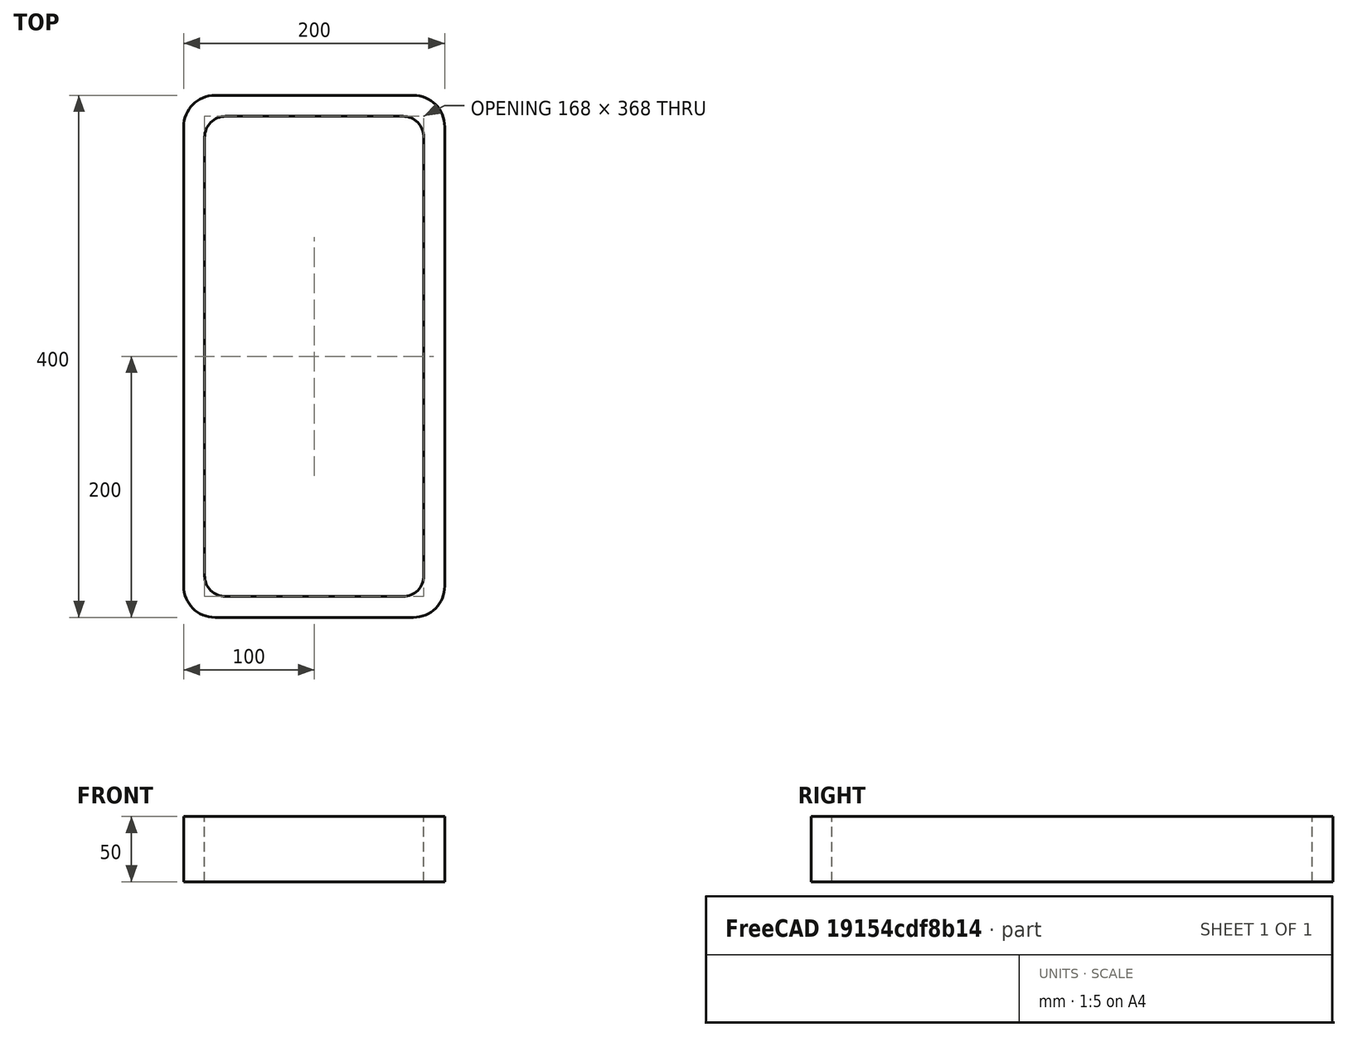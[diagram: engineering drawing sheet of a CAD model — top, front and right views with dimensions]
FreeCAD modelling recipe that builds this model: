
FCSTD DOCUMENT  (FreeCAD 0.15R4671 (Git))
Label: Rectangular hollow section 400x200x16 EN10219 S235JRH
License: All rights reserved
LicenseURL: http://en.wikipedia.org/wiki/All_rights_reserved
objects: Sketcher::SketchObject×1, Part::Extrusion×1
note: 2 computed .brp shape members not serialized (recipe doc carries the construction recipe); baked Part::Feature solids carry a one-line shape summary decoded from their .brp

FEATURE [Sketcher::SketchObject] Sketch
  sketch-geometry (16):
    g0: LineSegment StartX=-68 StartY=184 StartZ=0 EndX=68 EndY=184 EndZ=0
    g1: LineSegment StartX=84 StartY=168 StartZ=0 EndX=84 EndY=-168 EndZ=0
    g2: LineSegment StartX=68 StartY=-184 StartZ=0 EndX=-68 EndY=-184 EndZ=0
    g3: LineSegment StartX=-84 StartY=-168 StartZ=0 EndX=-84 EndY=168 EndZ=0
    g4: LineSegment StartX=-76 StartY=200 StartZ=0 EndX=76 EndY=200 EndZ=0
    g5: LineSegment StartX=100 StartY=176 StartZ=0 EndX=100 EndY=-176 EndZ=0
    g6: LineSegment StartX=76 StartY=-200 StartZ=0 EndX=-76 EndY=-200 EndZ=0
    g7: LineSegment StartX=-100 StartY=-176 StartZ=0 EndX=-100 EndY=176 EndZ=0
    g8: ArcOfCircle CenterX=-68 CenterY=168 CenterZ=0 NormalX=0 NormalY=0 NormalZ=1 Radius=16 StartAngle=1.5708 EndAngle=3.14159
    g9: ArcOfCircle CenterX=68 CenterY=168 CenterZ=0 NormalX=0 NormalY=0 NormalZ=1 Radius=16 StartAngle=0 EndAngle=1.5708
    g10: ArcOfCircle CenterX=68 CenterY=-168 CenterZ=0 NormalX=0 NormalY=0 NormalZ=1 Radius=16 StartAngle=4.71239 EndAngle=6.28319
    g11: ArcOfCircle CenterX=-68 CenterY=-168 CenterZ=0 NormalX=0 NormalY=0 NormalZ=1 Radius=16 StartAngle=3.14159 EndAngle=4.71239
    g12: ArcOfCircle CenterX=76 CenterY=176 CenterZ=0 NormalX=0 NormalY=0 NormalZ=1 Radius=24 StartAngle=0 EndAngle=1.5708
    g13: ArcOfCircle CenterX=76 CenterY=-176 CenterZ=0 NormalX=0 NormalY=0 NormalZ=1 Radius=24 StartAngle=4.71239 EndAngle=6.28319
    g14: ArcOfCircle CenterX=-76 CenterY=-176 CenterZ=0 NormalX=0 NormalY=0 NormalZ=1 Radius=24 StartAngle=3.14159 EndAngle=4.71239
    g15: ArcOfCircle CenterX=-76 CenterY=176 CenterZ=0 NormalX=0 NormalY=0 NormalZ=1 Radius=24 StartAngle=1.5708 EndAngle=3.14159
  constraints (36):
    c: Horizontal(g2)
    c: Vertical(g3)
    c: Horizontal(g6)
    c: Vertical(g7)
    c: Tangent(g3,g8) = 1.5708
    c: Tangent(g0,g8) = 1.5708
    c: Tangent(g0,g9) = 1.5708
    c: Tangent(g1,g9) = 1.5708
    c: Tangent(g1,g10) = 1.5708
    c: Tangent(g2,g10) = 1.5708
    c: Tangent(g2,g11) = 1.5708
    c: Tangent(g3,g11) = 1.5708
    c: Tangent(g4,g12) = 1.5708
    c: Tangent(g5,g12) = 1.5708
    c: Tangent(g5,g13) = 1.5708
    c: Tangent(g6,g13) = 1.5708
    c: Tangent(g6,g14) = 1.5708
    c: Tangent(g7,g14) = 1.5708
    c: Tangent(g7,g15) = 1.5708
    c: Tangent(g4,g15) = 1.5708
    c: Equal(g9,g8)
    c: Equal(g9,g11)
    c: Equal(g9,g10)
    c: Equal(g12,g15)
    c: Equal(g12,g14)
    c: Equal(g12,g13)
    c: Symmetric(g4,g6,g-1)
    c: Symmetric(g7,g5,g-2)
    c: DistanceY(g4,g6) = -400
    c: DistanceX(g7,g5) = 200
    c: Symmetric(g3,g1,g-2)
    c: Symmetric(g0,g2,g-1)
    c: DistanceY(g0,g4) = 16
    c: DistanceX(g5,g1) = -16
    c: Radius(g9) = 16
    c: Radius(g12) = 24
FEATURE [Part::Extrusion] Extrude  label="Rectangular hollow section 400x200x16 EN10219 S235JRH"
  Base = -> Sketch
  Dir = (0,0,50)
  Solid = true
